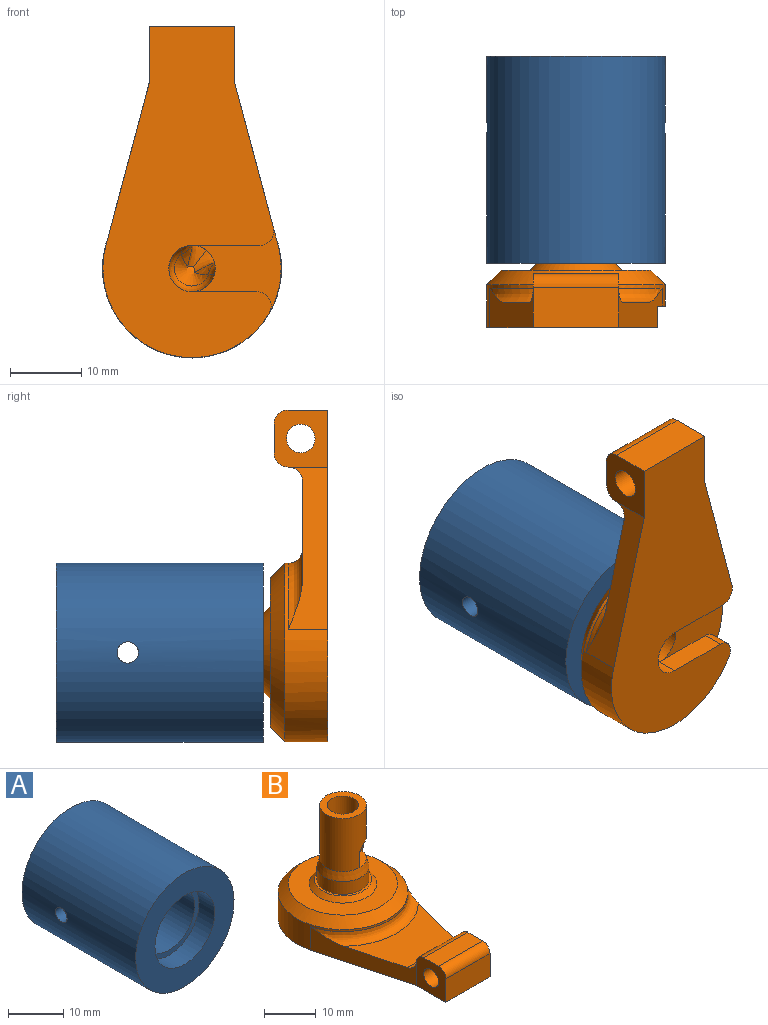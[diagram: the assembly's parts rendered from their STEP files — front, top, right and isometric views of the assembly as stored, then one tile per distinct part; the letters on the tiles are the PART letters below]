
ASSEMBLY  parts=2 mates=1
PART A: 8 faces, bbox 25.1x29x25.1 mm
  f0: cylinder r=12.55mm len=29mm, axis (0,1,0), area 2272.6mm2, adj f3,f5,f6,f7
  f1: cylinder r=6.5mm len=25mm, axis (0,-1,0), area 1006.8mm2, adj f4,f5,f6,f7
  f2: cylinder r=7.62mm len=15.25mm, axis (0,1,0), area 191.6mm2, adj f3,f4
  f3: plane 25.1x25.1mm, normal (0,-1,0), area 312.2mm2, adj f0,f2
  f4: plane 15.25x15.25mm, normal (0,-1,0), area 49.9mm2, adj f1,f2
  f5: plane 25.1x25.1mm, normal (0,1,0), area 362.1mm2, adj f0,f1
  f6: cylinder r=1.5mm len=6.23mm, axis (-1,0,0), area 57.4mm2, adj f0,f1
  f7: cylinder r=1.5mm len=6.23mm, axis (-1,0,0), area 57.4mm2, adj f0,f1
PART B: 44 faces, bbox 33.8x47x27 mm
  f0: plane 5.28x4.57mm, normal (0,0,1), area 7.4mm2, adj f2,f16,f34,f37
  f1: plane 46.5x23.97mm, normal (0,0,-1), area 732.3mm2, adj f2,f4,f6,f7,f8,f9,f10,f19
  f2: cylinder r=3.25mm len=14mm, axis (0,0,-1), area 235.3mm2, adj f0,f1,f19,f20,f21,f33,f34,f37
  f3: plane 20.37x13.68mm, normal (0,0,1), area 170.1mm2, adj f7,f8,f13,f23
  f4: cylinder r=12.5mm len=25mm, axis (0,0,-1), area 261.7mm2, adj f1,f7,f8,f13,f18,f21,f42
  f5: plane 21x21mm, normal (0,0,1), area 213.6mm2, adj f17,f18
  f6: plane 8x7.5mm, normal (-1,0,0), area 45.7mm2, adj f1,f7,f10,f11,f12,f22,f24
  f7: plane 23.24x6.54mm, normal (-0.97,-0.26,0), area 89mm2, adj f1,f3,f4,f6,f13,f23
  f8: plane 23.24x6.54mm, normal (0.97,-0.26,0), area 81.2mm2, adj f1,f3,f4,f9,f13,f21,f23,f43
  f9: plane 8x7.5mm, normal (1,0,0), area 45.7mm2, adj f1,f8,f10,f11,f12,f22,f24
  f10: plane 12x5.5mm, normal (0,-1,0), area 66mm2, adj f1,f6,f9,f24
  f11: plane 12x4mm, normal (0,0,1), area 48mm2, adj f6,f9,f22,f24
  f12: cylinder r=2mm len=12mm, axis (-1,0,0), area 150.8mm2, adj f6,f9
  f13: torus R=14.5mm, axis (0,0,-1), area 86.2mm2, adj f3,f4,f7,f8
  f14: plane 11x11mm, normal (0,0,1), area 16.5mm2, adj f15,f17
  f15: cylinder r=5mm len=10mm, axis (0,0,-1), area 94.2mm2, adj f14,f16
  f16: cone r=4.5mm half-angle=14deg, axis (0,0,-1), area 61.5mm2, adj f0,f15,f27
  f17: cone r=5.5mm half-angle=45deg, axis (0,0,-1), area 53.3mm2, adj f5,f14
  f18: cone r=10.5mm half-angle=45deg, axis (0,0,-1), area 204.4mm2, adj f4,f5
  f19: plane 9.46x3mm, normal (0,1,0), area 28.4mm2, adj f1,f2,f21,f43
  f20: plane 9.09x3mm, normal (0,-1,0), area 27.3mm2, adj f1,f2,f21,f42
  f21: plane 12.5x11.99mm, normal (0,0,-1), area 67.4mm2, adj f2,f4,f8,f19,f20,f42,f43
  f22: cylinder r=2mm len=12mm, axis (1,0,0), area 37.7mm2, adj f6,f9,f11,f23
  f23: cylinder r=2mm len=13.07mm, axis (1,0,0), area 39.4mm2, adj f3,f7,f8,f22
  f24: cylinder r=2mm len=12mm, axis (-1,0,0), area 37.7mm2, adj f6,f9,f10,f11
  f25: plane 0.89x0.64mm, normal (1,0,0), area 0.3mm2, adj f27,f36,f37,f38
  f26: plane 0.89x0.62mm, normal (-0.26,-0.97,0), area 0.3mm2, adj f27,f34,f35,f40
  f27: cylinder r=4.5mm len=12.5mm, axis (0,0,-1), area 325.5mm2, adj f16,f25,f26,f28,f31,f34,f37,f38
  f28: plane 1.58x1.5mm, normal (0,0,-1), area 1.2mm2, adj f27,f38,f39,f40,f41
  f29: cone r=3.25mm half-angle=32.6deg, axis (0,0,-1), area 18.1mm2, adj f33,f35,f36,f39,f41
  f30: cylinder r=3mm len=6mm, axis (0,0,-1), area 103.7mm2, adj f31,f32
  f31: plane 9x9mm, normal (0,0,1), area 35.3mm2, adj f27,f30
  f32: plane 6x6mm, normal (0,0,1), area 28.3mm2, adj f30
  f33: revolved ~6.4x6.1mm, area 32.6mm2, adj f2,f29,f34,f37
  f34: bspline ~6.31x3.29mm, area 6.7mm2, adj f0,f2,f26,f27,f33,f35
  f35: bspline ~6.29x4.84mm, area 5.5mm2, adj f26,f29,f34,f41
  f36: bspline ~6.29x5.16mm, area 5.5mm2, adj f25,f29,f37,f39
  f37: bspline ~6.31x3.79mm, area 6.7mm2, adj f0,f2,f25,f27,f33,f36
  f38: cylinder r=2mm len=2mm, axis (0,-1,0), area 1.7mm2, adj f25,f27,f28,f39
  f39: bspline ~4.33x2.61mm, area 8.6mm2, adj f28,f29,f36,f38,f41
  f40: cylinder r=2mm len=2.1mm, axis (-0.97,0.26,0), area 1.7mm2, adj f26,f27,f28,f41
  f41: bspline ~4.37x3.48mm, area 8.6mm2, adj f28,f29,f35,f39,f40
  f42: cylinder r=2mm len=3mm, axis (0,0,-1), area 12.6mm2, adj f1,f4,f20,f21
  f43: cylinder r=2mm len=3mm, axis (0,0,1), area 11mm2, adj f1,f8,f19,f21
PLACE A at identity fixed
PLACE B rot(axis=(-1,0,0),90deg) t=(0,-11.5,0)mm
MATE fastened B.f17 <-> A.f0  axis (0,1,0) through (0,-4,0)mm
